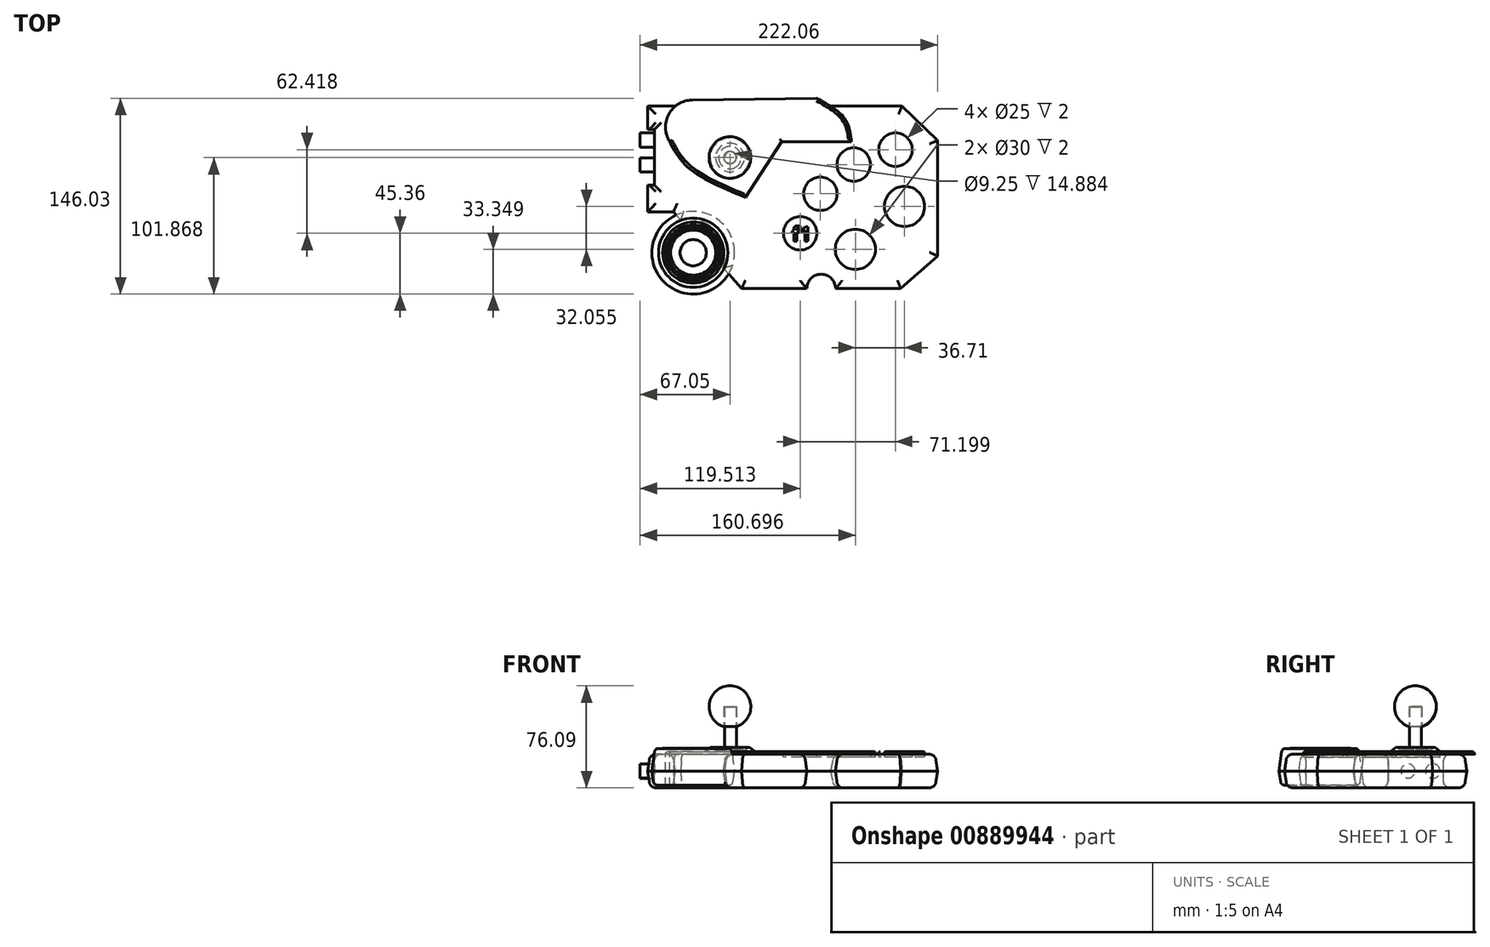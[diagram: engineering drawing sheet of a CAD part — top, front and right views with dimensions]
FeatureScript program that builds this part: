
annotation { "Feature Type Name" : "Feature", "Feature Type Description" : "" }
export const myFeature = defineFeature(function(context is Context, id is Id, definition is map)
    precondition{}
    {
        {
            var Q0;
            Q0=qCreatedBy(makeId("Top.planeOp"),FACE);
            var sketch = newSketch(context, id + "F0", { "sketchPlane" : qUnion([Q0])});
            skLineSegment(sketch, "E0", {"start": v(-138.95, 71.31) * mm, "end": v(27.52, 71.31) * mm});
            skLineSegment(sketch, "E1", {"start": v(27.52, 71.31) * mm, "end": v(54.11, 45.63) * mm});
            skLineSegment(sketch, "E2", {"start": v(54.11, 45.63) * mm, "end": v(54.11, -40.59) * mm});
            skLineSegment(sketch, "E3", {"start": v(54.11, -40.59) * mm, "end": v(26.6, -64.9) * mm});
            skLineSegment(sketch, "E4", {"start": v(26.6, -64.9) * mm, "end": v(-22.1, -64.9) * mm});
            skLineSegment(sketch, "E5", {"start": v(-92.18, -64.9) * mm, "end": v(-106.05, -49.27) * mm});
            skLineSegment(sketch, "E6", {"start": v(-143.08, -7.57) * mm, "end": v(-162.34, -7.57) * mm});
            skLineSegment(sketch, "E7", {"start": v(-162.34, -7.57) * mm, "end": v(-162.34, 71.31) * mm});
            skLineSegment(sketch, "E8", {"start": v(-162.34, 71.31) * mm, "end": v(-138.95, 71.31) * mm});
            skArc(sketch, "E9", {"start": v(-106.05, -49.27) * mm, "mid": v(-111.56, -22.37) * mm, "end": v(-137.62, -13.72) * mm});
            skLineSegment(sketch, "E10.trimOffspring", {"start": v(-137.62, -13.72) * mm, "end": v(-143.08, -7.57) * mm});
            skArc(sketch, "E11", {"start": v(-22.1, -64.9) * mm, "mid": v(-32.79, -54.2) * mm, "end": v(-43.48, -64.9) * mm});
            skLineSegment(sketch, "E12.trimOffspring", {"start": v(-43.48, -64.9) * mm, "end": v(-92.18, -64.9) * mm});
            skSolve(sketch);
        }
        {
            var Q0;
            Q0=makeQuery(id+"F0.imprint","IMPRINT",FACE,{"disambiguationData":[TD([[makeQuery(id+"F0.imprint","IMPRINT",EDGE,{"derivedFrom":sQuery(id+"F0.wireOp",EDGE,"E0")}),-1.0]])]});
            extrude(context, id + "F1", {"entities" : qUnion([Q0]), "endBound" : BoundingType.SYMMETRIC, "depth" : 25 * mm, "offsetDistance" : 25 * mm, "hasDraft" : true, "draftAngle" : 8 * degree, "draftPullDirection" : true});
        }
        {
            var Q0;
            Q0=qCreatedBy(makeId("Top.planeOp"),FACE);
            var sketch = newSketch(context, id + "F2", { "sketchPlane" : qUnion([Q0])});
            skCircle(sketch, "E13", {"center": v(-128.34, -38.14) * mm, "radius": 30.86 * mm});
            skSolve(sketch);
        }
        {
            var Q0;
            Q0=makeQuery(id+"F2.imprint","IMPRINT",FACE,{"disambiguationData":[TD([[makeQuery(id+"F2.imprint","IMPRINT",EDGE,{"derivedFrom":sQuery(id+"F2.wireOp",EDGE,"E13")}),1.0]])]});
            extrude(context, id + "F3", {"entities" : qUnion([Q0]), "depth" : 17 * mm, "offsetDistance" : 25 * mm, "hasDraft" : true, "draftAngle" : 8 * degree, "draftPullDirection" : true, "hasSecondDirection" : true, "secondDirectionOppositeDirection" : true, "secondDirectionDepth" : 10.5 * mm, "hasSecondDirectionDraft" : true, "secondDirectionDraftAngle" : 8 * degree, "secondDirectionDraftPullDirection" : true});
        }
        {
            var Q0;
            Q0=makeQuery(id+"F3.opExtrude","CAP_EDGE",EDGE,{"disambiguationData":[OSD([sQuery(id+"F2.wireOp",EDGE,"E13")])],"isStart":false});
            var Q1;
            Q1=makeQuery(id+"F3.opExtrude","CAP_EDGE",EDGE,{"disambiguationData":[OSD([sQuery(id+"F2.wireOp",EDGE,"E13")])],"isStart":true});
            fillet(context, id + "F4", {"entities" : qUnion([Q0, Q1]), "radius" : 3 * mm, "tangentPropagation" : true, "allowEdgeOverflow" : false});
        }
        {
            var Q0;
            Q0=makeQuery(id+"F1.opExtrude","CAP_FACE",FACE,{"disambiguationData":[OSD([sQuery(id+"F0.wireOp",EDGE,"E0"),sQuery(id+"F0.wireOp",EDGE,"E1"),sQuery(id+"F0.wireOp",EDGE,"E2"),sQuery(id+"F0.wireOp",EDGE,"E3"),sQuery(id+"F0.wireOp",EDGE,"E4"),sQuery(id+"F0.wireOp",EDGE,"E5"),sQuery(id+"F0.wireOp",EDGE,"E6"),sQuery(id+"F0.wireOp",EDGE,"E7"),sQuery(id+"F0.wireOp",EDGE,"E8"),sQuery(id+"F0.wireOp",EDGE,"E9"),sQuery(id+"F0.wireOp",EDGE,"E10.trimOffspring"),sQuery(id+"F0.wireOp",EDGE,"E11"),sQuery(id+"F0.wireOp",EDGE,"E12.trimOffspring")])],"isStart":false});
            var sketch = newSketch(context, id + "F5", { "sketchPlane" : qUnion([Q0])});
            skArc(sketch, "E14", {"start": v(-129.09, 75.83) * mm, "mid": v(-146.6, 65.29) * mm, "end": v(-145.98, 44.85) * mm});
            skFitSpline(sketch, "E15", {"points": [v(-147.89, 48.78) * mm, v(-132.7, 26.03) * mm, v(-89.4, 3.14) * mm], "startDerivative": vector(26.9, -56.04) * mm, "endDerivative": vector(87.17, -36.2) * mm});
            skLineSegment(sketch, "E16", {"start": v(-89.4, 3.14) * mm, "end": v(-62.29, 44.68) * mm});
            skLineSegment(sketch, "E17", {"start": v(-62.29, 44.68) * mm, "end": v(-10.18, 44.68) * mm});
            skFitSpline(sketch, "E18", {"points": [v(-10.18, 44.68) * mm, v(-15.81, 62.64) * mm, v(-45.74, 82) * mm], "startDerivative": vector(-5.33, 44.6) * mm, "endDerivative": vector(-62.76, 30.76) * mm});
            skLineSegment(sketch, "E19", {"start": v(-129.09, 75.83) * mm, "end": v(-35.8, 77.03) * mm});
            skSolve(sketch);
        }
        {
            var Q0;
            Q0 = qSketchRegion(id + "F5", true);
            extrude(context, id + "F6", {"entities" : qUnion([Q0]), "depth" : 2 * mm, "offsetDistance" : 25 * mm, "hasSecondDirection" : true, "secondDirectionOppositeDirection" : true, "secondDirectionDepth" : 25 * mm});
        }
        {
            var Q0;
            Q0=makeQuery(id+"F1.opExtrude","CAP_FACE",FACE,{"disambiguationData":[OSD([sQuery(id+"F0.wireOp",EDGE,"E0"),sQuery(id+"F0.wireOp",EDGE,"E1"),sQuery(id+"F0.wireOp",EDGE,"E2"),sQuery(id+"F0.wireOp",EDGE,"E3"),sQuery(id+"F0.wireOp",EDGE,"E4"),sQuery(id+"F0.wireOp",EDGE,"E5"),sQuery(id+"F0.wireOp",EDGE,"E6"),sQuery(id+"F0.wireOp",EDGE,"E7"),sQuery(id+"F0.wireOp",EDGE,"E8"),sQuery(id+"F0.wireOp",EDGE,"E9"),sQuery(id+"F0.wireOp",EDGE,"E10.trimOffspring"),sQuery(id+"F0.wireOp",EDGE,"E11"),sQuery(id+"F0.wireOp",EDGE,"E12.trimOffspring")])],"isStart":false});
            var sketch = newSketch(context, id + "F7", { "sketchPlane" : qUnion([Q0])});
            skLineSegment(sketch, "E20", {"start": v(-170.55, 53.82) * mm, "end": v(-157.35, 53.82) * mm});
            skLineSegment(sketch, "E21", {"start": v(-157.35, 53.82) * mm, "end": v(-157.35, 12.42) * mm});
            skLineSegment(sketch, "E22", {"start": v(-157.35, 12.42) * mm, "end": v(-175.2, 12.42) * mm});
            skLineSegment(sketch, "E23", {"start": v(-175.2, 12.42) * mm, "end": v(-170.55, 53.82) * mm});
            skSolve(sketch);
        }
        {
            var Q0;
            Q0 = qSketchRegion(id + "F7", true);
            extrude(context, id + "F8", {"entities" : qUnion([Q0]), "operationType" : NewBodyOperationType.REMOVE, "oppositeDirection" : true, "depth" : 25 * mm, "offsetDistance" : 25 * mm});
        }
        {
            var Q0;
            Q0=makeQuery(id+"F8.boolean.opBoolean","COPY",FACE,{"derivedFrom":makeQuery(id+"F8.opExtrude","SWEPT_FACE",FACE,{"disambiguationData":[OSD([sQuery(id+"F7.wireOp",EDGE,"E21")])]})});
            var sketch = newSketch(context, id + "F9", { "sketchPlane" : qUnion([Q0])});
            skCircle(sketch, "E24", {"center": v(-45.8, 0) * mm, "radius": 5.4 * mm});
            skPoint(sketch, "E24.centerSnap0", {"position": v(-53.82, 0) * mm});
            skCircle(sketch, "E25", {"center": v(-27.39, 0) * mm, "radius": 5.26 * mm});
            skSolve(sketch);
        }
        {
            var Q0;
            Q0=makeQuery(id+"F9.imprint","IMPRINT",FACE,{"disambiguationData":[TD([[makeQuery(id+"F9.imprint","IMPRINT",EDGE,{"derivedFrom":sQuery(id+"F9.wireOp",EDGE,"E25")}),1.0]])]});
            var Q1;
            Q1=makeQuery(id+"F9.imprint","IMPRINT",FACE,{"disambiguationData":[TD([[makeQuery(id+"F9.imprint","IMPRINT",EDGE,{"derivedFrom":sQuery(id+"F9.wireOp",EDGE,"E24")}),1.0]])]});
            extrude(context, id + "F10", {"entities" : qUnion([Q0, Q1]), "depth" : 10.6 * mm, "offsetDistance" : 25 * mm});
        }
        {
            var Q0;
            Q0=makeQuery(id+"F1.opExtrude","CAP_EDGE",EDGE,{"disambiguationData":[OSD([sQuery(id+"F0.wireOp",EDGE,"E2")])],"isStart":false});
            var Q1;
            Q1=makeQuery(id+"F1.opExtrude","CAP_EDGE",EDGE,{"disambiguationData":[OSD([sQuery(id+"F0.wireOp",EDGE,"E3")])],"isStart":false});
            var Q2;
            Q2=makeQuery(id+"F1.opExtrude","CAP_FACE",FACE,{"disambiguationData":[OSD([sQuery(id+"F0.wireOp",EDGE,"E0"),sQuery(id+"F0.wireOp",EDGE,"E1"),sQuery(id+"F0.wireOp",EDGE,"E2"),sQuery(id+"F0.wireOp",EDGE,"E3"),sQuery(id+"F0.wireOp",EDGE,"E4"),sQuery(id+"F0.wireOp",EDGE,"E5"),sQuery(id+"F0.wireOp",EDGE,"E6"),sQuery(id+"F0.wireOp",EDGE,"E7"),sQuery(id+"F0.wireOp",EDGE,"E8"),sQuery(id+"F0.wireOp",EDGE,"E9"),sQuery(id+"F0.wireOp",EDGE,"E10.trimOffspring"),sQuery(id+"F0.wireOp",EDGE,"E11"),sQuery(id+"F0.wireOp",EDGE,"E12.trimOffspring")])],"isStart":false});
            var Q3;
            Q3=makeQuery(id+"F1.opExtrude","CAP_FACE",FACE,{"disambiguationData":[OSD([sQuery(id+"F0.wireOp",EDGE,"E0"),sQuery(id+"F0.wireOp",EDGE,"E1"),sQuery(id+"F0.wireOp",EDGE,"E2"),sQuery(id+"F0.wireOp",EDGE,"E3"),sQuery(id+"F0.wireOp",EDGE,"E4"),sQuery(id+"F0.wireOp",EDGE,"E5"),sQuery(id+"F0.wireOp",EDGE,"E6"),sQuery(id+"F0.wireOp",EDGE,"E7"),sQuery(id+"F0.wireOp",EDGE,"E8"),sQuery(id+"F0.wireOp",EDGE,"E9"),sQuery(id+"F0.wireOp",EDGE,"E10.trimOffspring"),sQuery(id+"F0.wireOp",EDGE,"E11"),sQuery(id+"F0.wireOp",EDGE,"E12.trimOffspring")])],"isStart":true});
            fillet(context, id + "F11", {"entities" : qUnion([Q0, Q1, Q2, Q3]), "radius" : 5 * mm, "tangentPropagation" : true, "allowEdgeOverflow" : false});
        }
        {
            var Q0;
            Q0=makeQuery(id+"F6.opExtrude","CAP_FACE",FACE,{"disambiguationData":[OSD([sQuery(id+"F5.wireOp",EDGE,"E14"),sQuery(id+"F5.wireOp",EDGE,"E15"),sQuery(id+"F5.wireOp",EDGE,"E16"),sQuery(id+"F5.wireOp",EDGE,"E17"),sQuery(id+"F5.wireOp",EDGE,"E18"),sQuery(id+"F5.wireOp",EDGE,"E19")])],"isStart":false});
            var sketch = newSketch(context, id + "F12", { "sketchPlane" : qUnion([Q0])});
            skCircle(sketch, "E26", {"center": v(-100.38, 32.9) * mm, "radius": 4.42 * mm});
            skSolve(sketch);
        }
        {
            var Q0;
            Q0 = qSketchRegion(id + "F12", true);
            extrude(context, id + "F13", {"entities" : qUnion([Q0]), "depth" : 33.3 * mm, "offsetDistance" : 25 * mm});
        }
        {
            var Q0;
            Q0=qCreatedBy(makeId("Right.planeOp"),FACE);
            cPlane(context, id + "F14", {"entities" : qUnion([Q0]), "cplaneType" : CPlaneType.OFFSET, "offset" : 100.9 * mm, "oppositeDirection" : true, "width" : 150 * mm, "height" : 150 * mm});
        }
        {
            var Q0;
            Q0=qCreatedBy(id+"F14.planeOp",FACE);
            var sketch = newSketch(context, id + "F15", { "sketchPlane" : qUnion([Q0])});
            skLineSegment(sketch, "E27", {"start": v(37.32, 14.46) * mm, "end": v(41.24, 16.74) * mm});
            skLineSegment(sketch, "E28", {"start": v(41.24, 16.74) * mm, "end": v(43.53, 15.3) * mm});
            skLineSegment(sketch, "E29", {"start": v(43.53, 15.3) * mm, "end": v(47.56, 17.63) * mm});
            skLineSegment(sketch, "E30", {"start": v(51.37, 14.34) * mm, "end": v(37.32, 14.46) * mm});
            skLineSegment(sketch, "E31", {"start": v(32.84, 14.46) * mm, "end": v(32.84, 21.13) * mm, "construction": true});
            skLineSegment(sketch, "E32", {"start": v(51.37, 14.34) * mm, "end": v(47.56, 17.63) * mm});
            skPoint(sketch, "E32.endSnap0", {"position": v(46.96, 17.28) * mm});
            skPoint(sketch, "E33.start.orphan", {"position": v(50.39, 19.26) * mm});
            skPoint(sketch, "E34.orphan", {"position": v(46.96, 18.14) * mm});
            skSolve(sketch);
        }
        {
            var Q0;
            Q0 = qSketchRegion(id + "F15", true);
            var Q1;
            Q1=sQuery(id+"F15.wireOp",EDGE,"E31");
            revolve(context, id + "F16", {"operationType" : NewBodyOperationType.ADD, "surfaceOperationType" : NewSurfaceOperationType.NEW, "entities" : qUnion([Q0]), "axis" : qUnion([Q1]), "revolveType" : RevolveType.FULL});
        }
        {
            var Q0;
            Q0=qCreatedBy(id+"F14.planeOp",FACE);
            var sketch = newSketch(context, id + "F17", { "sketchPlane" : qUnion([Q0])});
            skArc(sketch, "E35", {"start": v(32.87, 63.59) * mm, "mid": v(17.46, 50.34) * mm, "end": v(28.24, 33.12) * mm});
            skLineSegment(sketch, "E36", {"start": v(32.87, 48) * mm, "end": v(28.24, 48) * mm});
            skLineSegment(sketch, "E37", {"start": v(28.24, 48) * mm, "end": v(28.24, 33.12) * mm});
            skLineSegment(sketch, "E38", {"start": v(32.87, 48) * mm, "end": v(32.87, 63.59) * mm});
            skSolve(sketch);
        }
        {
            var Q0;
            Q0=makeQuery(id+"F17.imprint","IMPRINT",FACE,{"disambiguationData":[TD([[makeQuery(id+"F17.imprint","IMPRINT",EDGE,{"derivedFrom":sQuery(id+"F17.wireOp",EDGE,"E35")}),1.0]])]});
            var Q1;
            Q1=sQuery(id+"F17.wireOp",EDGE,"E38");
            revolve(context, id + "F18", {"surfaceOperationType" : NewSurfaceOperationType.NEW, "entities" : qUnion([Q0]), "axis" : qUnion([Q1]), "revolveType" : RevolveType.FULL});
        }
        {
            var Q0;
            Q0=makeQuery(id+"F3.opExtrude","CAP_FACE",FACE,{"disambiguationData":[OSD([sQuery(id+"F2.wireOp",EDGE,"E13")])],"isStart":false});
            var sketch = newSketch(context, id + "F19", { "sketchPlane" : qUnion([Q0])});
            skCircle(sketch, "E39", {"center": v(-128.34, -38.14) * mm, "radius": 20.8 * mm});
            skCircle(sketch, "E40.0", {"center": v(-128.34, -38.14) * mm, "radius": 18.8 * mm});
            skCircle(sketch, "E41.0", {"center": v(-128.34, -38.14) * mm, "radius": 16.8 * mm});
            skCircle(sketch, "E42.0", {"center": v(-128.34, -38.14) * mm, "radius": 22.8 * mm});
            skCircle(sketch, "E43.0", {"center": v(-128.34, -38.14) * mm, "radius": 9.8 * mm});
            skSolve(sketch);
        }
        {
            var Q0;
            Q0=makeQuery(id+"F19.imprint","IMPRINT",FACE,{"disambiguationData":[TD([[makeQuery(id+"F19.imprint","IMPRINT",EDGE,{"derivedFrom":sQuery(id+"F19.wireOp",EDGE,"E41.0")}),1.0]])]});
            var Q1;
            Q1=makeQuery(id+"F19.imprint","IMPRINT",FACE,{"disambiguationData":[TD([[makeQuery(id+"F19.imprint","IMPRINT",EDGE,{"derivedFrom":sQuery(id+"F19.wireOp",EDGE,"E39")}),1.0]])]});
            var Q2;
            Q2=makeQuery(id+"F19.imprint","IMPRINT",FACE,{"disambiguationData":[TD([[makeQuery(id+"F19.imprint","IMPRINT",EDGE,{"derivedFrom":sQuery(id+"F19.wireOp",EDGE,"E42.0")}),-1.0]])]});
            extrude(context, id + "F20", {"entities" : qUnion([Q0, Q1, Q2]), "operationType" : NewBodyOperationType.REMOVE, "oppositeDirection" : true, "depth" : .5 * mm, "offsetDistance" : 25 * mm});
        }
        {
            var Q0;
            Q0=makeQuery(id+"F1.opExtrude","CAP_FACE",FACE,{"disambiguationData":[OSD([sQuery(id+"F0.wireOp",EDGE,"E0"),sQuery(id+"F0.wireOp",EDGE,"E1"),sQuery(id+"F0.wireOp",EDGE,"E2"),sQuery(id+"F0.wireOp",EDGE,"E3"),sQuery(id+"F0.wireOp",EDGE,"E4"),sQuery(id+"F0.wireOp",EDGE,"E5"),sQuery(id+"F0.wireOp",EDGE,"E6"),sQuery(id+"F0.wireOp",EDGE,"E7"),sQuery(id+"F0.wireOp",EDGE,"E8"),sQuery(id+"F0.wireOp",EDGE,"E9"),sQuery(id+"F0.wireOp",EDGE,"E10.trimOffspring"),sQuery(id+"F0.wireOp",EDGE,"E11"),sQuery(id+"F0.wireOp",EDGE,"E12.trimOffspring")])],"isStart":false});
            var sketch = newSketch(context, id + "F21", { "sketchPlane" : qUnion([Q0])});
            skCircle(sketch, "E44", {"center": v(36.15, -48.31) * mm, "radius": 88.11 * mm, "construction": true});
            skCircle(sketch, "E45", {"center": v(36.15, -48.31) * mm, "radius": 45.21 * mm, "construction": true});
            skCircle(sketch, "E46", {"center": v(-48.44, -23.64) * mm, "radius": 12.5 * mm});
            skCircle(sketch, "E47.1.0", {"center": v(-33.35, 5.85) * mm, "radius": 12.5 * mm});
            skCircle(sketch, "E47.2.0", {"center": v(-8.45, 27.68) * mm, "radius": 12.5 * mm});
            skCircle(sketch, "E47.3.0", {"center": v(22.76, 38.78) * mm, "radius": 12.5 * mm});
            skLineSegment(sketch, "E47.anchor1", {"start": v(36.15, -48.31) * mm, "end": v(-48.44, -23.64) * mm, "construction": true});
            skLineSegment(sketch, "E47.anchor2", {"start": v(36.15, -48.31) * mm, "end": v(22.76, 38.78) * mm, "construction": true});
            skCircle(sketch, "E48", {"center": v(-7.25, -35.65) * mm, "radius": 15 * mm});
            skCircle(sketch, "E49", {"center": v(29.46, -3.6) * mm, "radius": 15 * mm});
            skPoint(sketch, "E49.centerSnap0", {"position": v(29.46, -4.77) * mm});
            skSolve(sketch);
        }
        {
            var Q0;
            Q0=makeQuery(id+"F21.imprint","IMPRINT",FACE,{"disambiguationData":[TD([[makeQuery(id+"F21.imprint","IMPRINT",EDGE,{"derivedFrom":sQuery(id+"F21.wireOp",EDGE,"E46")}),1.0]])]});
            var Q1;
            Q1=makeQuery(id+"F21.imprint","IMPRINT",FACE,{"disambiguationData":[TD([[makeQuery(id+"F21.imprint","IMPRINT",EDGE,{"derivedFrom":sQuery(id+"F21.wireOp",EDGE,"E47.1.0")}),1.0]])]});
            var Q2;
            Q2=makeQuery(id+"F21.imprint","IMPRINT",FACE,{"disambiguationData":[TD([[makeQuery(id+"F21.imprint","IMPRINT",EDGE,{"derivedFrom":sQuery(id+"F21.wireOp",EDGE,"E47.2.0")}),1.0]])]});
            var Q3;
            Q3=makeQuery(id+"F21.imprint","IMPRINT",FACE,{"disambiguationData":[TD([[makeQuery(id+"F21.imprint","IMPRINT",EDGE,{"derivedFrom":sQuery(id+"F21.wireOp",EDGE,"E47.3.0")}),1.0]])]});
            var Q4;
            Q4=makeQuery(id+"F21.imprint","IMPRINT",FACE,{"disambiguationData":[TD([[makeQuery(id+"F21.imprint","IMPRINT",EDGE,{"derivedFrom":sQuery(id+"F21.wireOp",EDGE,"E49")}),1.0]])]});
            var Q5;
            Q5=makeQuery(id+"F21.imprint","IMPRINT",FACE,{"disambiguationData":[TD([[makeQuery(id+"F21.imprint","IMPRINT",EDGE,{"derivedFrom":sQuery(id+"F21.wireOp",EDGE,"E48")}),1.0]])]});
            extrude(context, id + "F22", {"entities" : qUnion([Q0, Q1, Q2, Q3, Q4, Q5]), "operationType" : NewBodyOperationType.REMOVE, "oppositeDirection" : true, "depth" : 2 * mm, "offsetDistance" : 25 * mm});
        }
        {
            var Q0;
            Q0=makeQuery(id+"F22.boolean.opBoolean","COPY",FACE,{"derivedFrom":makeQuery(id+"F22.opExtrude","CAP_FACE",FACE,{"disambiguationData":[OSD([sQuery(id+"F21.wireOp",EDGE,"E46")])],"isStart":false})});
            var Q1;
            Q1=makeQuery(id+"F22.boolean.opBoolean","COPY",FACE,{"derivedFrom":makeQuery(id+"F22.opExtrude","CAP_FACE",FACE,{"disambiguationData":[OSD([sQuery(id+"F21.wireOp",EDGE,"E47.1.0")])],"isStart":false})});
            var Q2;
            Q2=makeQuery(id+"F22.boolean.opBoolean","COPY",FACE,{"derivedFrom":makeQuery(id+"F22.opExtrude","CAP_FACE",FACE,{"disambiguationData":[OSD([sQuery(id+"F21.wireOp",EDGE,"E47.2.0")])],"isStart":false})});
            var Q3;
            Q3=makeQuery(id+"F22.boolean.opBoolean","COPY",FACE,{"derivedFrom":makeQuery(id+"F22.opExtrude","CAP_FACE",FACE,{"disambiguationData":[OSD([sQuery(id+"F21.wireOp",EDGE,"E47.3.0")])],"isStart":false})});
            var Q4;
            Q4=makeQuery(id+"F22.boolean.opBoolean","COPY",FACE,{"derivedFrom":makeQuery(id+"F22.opExtrude","CAP_FACE",FACE,{"disambiguationData":[OSD([sQuery(id+"F21.wireOp",EDGE,"E48")])],"isStart":false})});
            var Q5;
            Q5=makeQuery(id+"F22.boolean.opBoolean","COPY",FACE,{"derivedFrom":makeQuery(id+"F22.opExtrude","CAP_FACE",FACE,{"disambiguationData":[OSD([sQuery(id+"F21.wireOp",EDGE,"E49")])],"isStart":false})});
            extrude(context, id + "F23", {"entities" : qUnion([Q0, Q1, Q2, Q3, Q4, Q5]), "depth" : 4 * mm, "offsetDistance" : 25 * mm});
        }
        {
            var Q0;
            Q0=makeQuery(id+"F23.opExtrude","CAP_EDGE",EDGE,{"disambiguationData":[OSD([sQuery(id+"F21.wireOp",EDGE,"E46")])],"isStart":false});
            var Q1;
            Q1=makeQuery(id+"F23.opExtrude","CAP_EDGE",EDGE,{"disambiguationData":[OSD([sQuery(id+"F21.wireOp",EDGE,"E47.1.0")])],"isStart":false});
            var Q2;
            Q2=makeQuery(id+"F23.opExtrude","CAP_EDGE",EDGE,{"disambiguationData":[OSD([sQuery(id+"F21.wireOp",EDGE,"E47.2.0")])],"isStart":false});
            var Q3;
            Q3=makeQuery(id+"F23.opExtrude","CAP_EDGE",EDGE,{"disambiguationData":[OSD([sQuery(id+"F21.wireOp",EDGE,"E47.3.0")])],"isStart":false});
            var Q4;
            Q4=makeQuery(id+"F23.opExtrude","CAP_EDGE",EDGE,{"disambiguationData":[OSD([sQuery(id+"F21.wireOp",EDGE,"E49")])],"isStart":false});
            var Q5;
            Q5=makeQuery(id+"F23.opExtrude","CAP_EDGE",EDGE,{"disambiguationData":[OSD([sQuery(id+"F21.wireOp",EDGE,"E48")])],"isStart":false});
            fillet(context, id + "F24", {"entities" : qUnion([Q0, Q1, Q2, Q3, Q4, Q5]), "radius" : 1 * mm, "tangentPropagation" : true, "allowEdgeOverflow" : false});
        }
        {
            var Q0;
            Q0 = qSketchRegion(id + "F5", true);
            extrude(context, id + "F25", {"entities" : qUnion([Q0]), "operationType" : NewBodyOperationType.REMOVE, "oppositeDirection" : true, "depth" : 25 * mm, "offsetDistance" : 25 * mm});
        }
        {
            var Q0;
            {var subQ0=sQuery(id+"F5.wireOp",EDGE,"E16");var subQ1=sQuery(id+"F5.wireOp",EDGE,"E15");var subQ2=sQuery(id+"F5.wireOp",EDGE,"E17");var subQ3=sQuery(id+"F5.wireOp",EDGE,"E14");var subQ4=sQuery(id+"F5.wireOp",EDGE,"E18");var subQ5=sQuery(id+"F5.wireOp",EDGE,"E19");Q0=makeQuery(id+"F16.boolean.opBoolean","SPLIT",FACE,{"disambiguationData":[TD([makeQuery(id+"F6.opExtrude","SWEPT_FACE",FACE,{"disambiguationData":[OSD([subQ3])]})])],"derivedFrom":makeQuery(id+"F6.opExtrude","CAP_FACE",FACE,{"disambiguationData":[OSD([subQ3,subQ1,subQ0,subQ2,subQ4,subQ5])],"isStart":false})});}
            var Q1;
            Q1=makeQuery(id+"F6.opExtrude","CAP_EDGE",EDGE,{"disambiguationData":[OSD([sQuery(id+"F5.wireOp",EDGE,"E19")])],"isStart":true});
            var Q2;
            Q2=makeQuery(id+"F6.opExtrude","CAP_EDGE",EDGE,{"disambiguationData":[OSD([sQuery(id+"F5.wireOp",EDGE,"E18")])],"isStart":true});
            var Q3;
            Q3=makeQuery(id+"F6.opExtrude","SWEPT_EDGE",EDGE,{"disambiguationData":[OSD([sQuery(id+"F5.wireOp",EDGE,"E18"),sQuery(id+"F5.wireOp",EDGE,"E19")])]});
            fillet(context, id + "F26", {"entities" : qUnion([Q0, Q1, Q2, Q3]), "radius" : 2 * mm, "allowEdgeOverflow" : false});
        }
        {
            var Q0;
            Q0=makeQuery(id+"F23.opExtrude","CAP_FACE",FACE,{"disambiguationData":[OSD([sQuery(id+"F21.wireOp",EDGE,"E46")])],"isStart":false});
            var sketch = newSketch(context, id + "F27", { "sketchPlane" : qUnion([Q0])});
            skText(sketch, "E50", { "text": "f1", "fontName": "OpenSans-Bold.ttf"});
            const initialGuessF27  = {"E50": [-0.0547, -0.02953, 1, 0, 0.01078]};
            skSetInitialGuess(sketch, initialGuessF27);
            skSolve(sketch);
        }
        {
            var Q0;
            Q0 = qSketchRegion(id + "F27", true);
            extrude(context, id + "F28", {"entities" : qUnion([Q0]), "operationType" : NewBodyOperationType.REMOVE, "oppositeDirection" : true, "depth" : .5 * mm, "offsetDistance" : 25 * mm});
        }
        {
            var Q0;
            Q0=makeQuery(id+"F20.boolean.opBoolean","SPLIT",FACE,{"disambiguationData":[TD([makeQuery(id+"F20.opExtrude","SWEPT_FACE",FACE,{"disambiguationData":[OSD([sQuery(id+"F19.wireOp",EDGE,"E43.0")])]})])],"derivedFrom":makeQuery(id+"F3.opExtrude","CAP_FACE",FACE,{"disambiguationData":[OSD([sQuery(id+"F2.wireOp",EDGE,"E13")])],"isStart":false})});
            var Q1;
            Q1=makeQuery(id+"F20.boolean.opBoolean","COPY",EDGE,{"derivedFrom":makeQuery(id+"F20.opExtrude","CAP_EDGE",EDGE,{"disambiguationData":[OSD([sQuery(id+"F19.wireOp",EDGE,"E41.0")])],"isStart":true})});
            var Q2;
            Q2=makeQuery(id+"F20.boolean.opBoolean","COPY",EDGE,{"derivedFrom":makeQuery(id+"F20.opExtrude","CAP_EDGE",EDGE,{"disambiguationData":[OSD([sQuery(id+"F19.wireOp",EDGE,"E39")])],"isStart":true})});
            var Q3;
            {var subQ0=sQuery(id+"F2.wireOp",EDGE,"E13");Q3=makeQuery(id+"F20.boolean.opBoolean","MERGE",EDGE,{"derivedFrom":[makeQuery(id+"F4.opFillet","BLEND_EDGE",EDGE,{"blendedFrom":[makeQuery(id+"F3.opExtrude","CAP_EDGE",EDGE,{"disambiguationData":[OSD([subQ0])],"isStart":false}),makeQuery(id+"F3.opExtrude","CAP_FACE",FACE,{"disambiguationData":[OSD([subQ0])],"isStart":false})],"blendedInto":[makeQuery(id+"F3.opExtrude","CAP_FACE",FACE,{"disambiguationData":[OSD([subQ0])],"isStart":false})]})],"fromTools":[makeQuery(id+"F20.opExtrude","CAP_EDGE",EDGE,{"disambiguationData":[OSD([subQ0])],"isStart":true})]});}
            fillet(context, id + "F29", {"entities" : qUnion([Q0, Q1, Q2, Q3]), "radius" : 1 * mm, "tangentPropagation" : true, "allowEdgeOverflow" : false});
        }
    });
